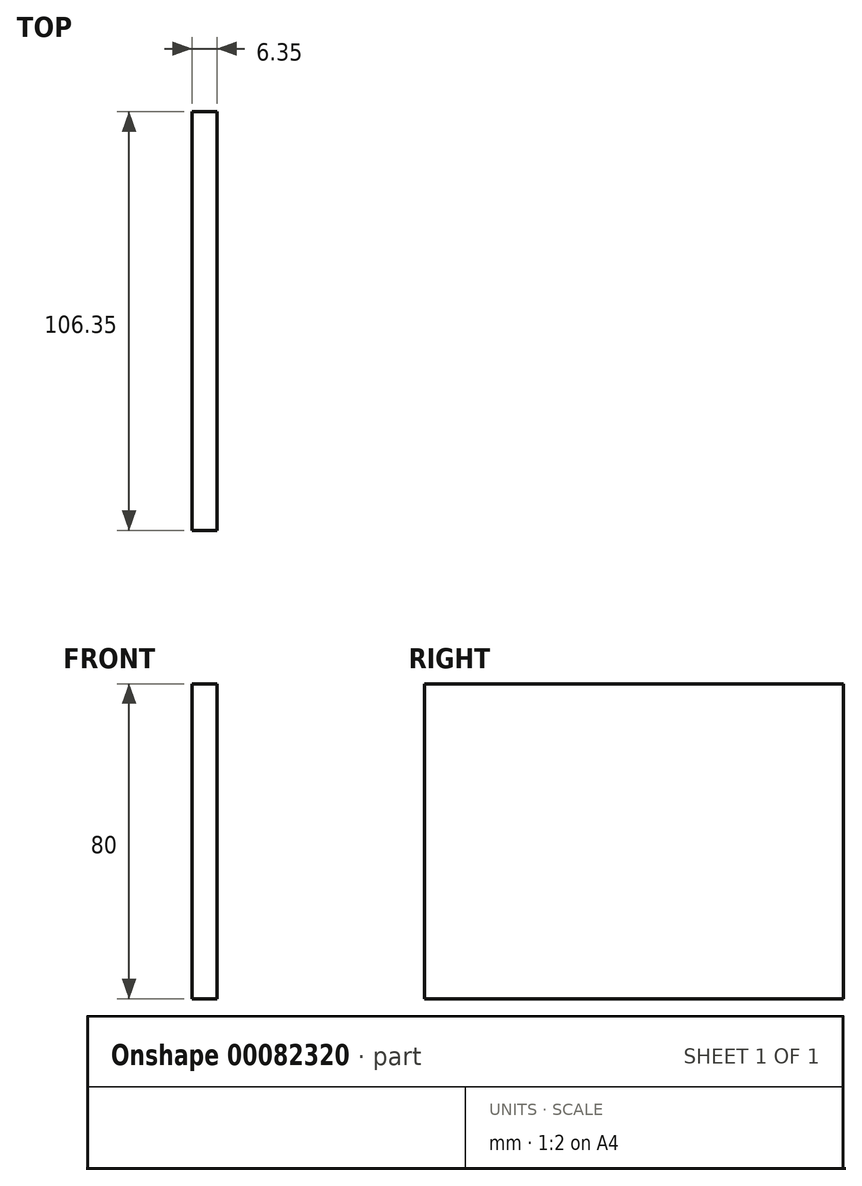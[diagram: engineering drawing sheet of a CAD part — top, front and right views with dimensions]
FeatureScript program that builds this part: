
annotation { "Feature Type Name" : "Feature", "Feature Type Description" : "" }
export const myFeature = defineFeature(function(context is Context, id is Id, definition is map)
    precondition{}
    {
        {
            var Q0;
            Q0=qCreatedBy(makeId("Right.planeOp"),FACE);
            var sketch = newSketch(context, id + "F0", { "sketchPlane" : qUnion([Q0])});
            skLineSegment(sketch, "E0.bottom", {"start": v(50, -37.5) * mm, "end": v(-50, -37.5) * mm});
            skLineSegment(sketch, "E0.top", {"start": v(50, 37.5) * mm, "end": v(-50, 37.5) * mm});
            skLineSegment(sketch, "E0.left", {"start": v(50, -37.5) * mm, "end": v(50, 37.5) * mm});
            skLineSegment(sketch, "E0.right", {"start": v(-50, -37.5) * mm, "end": v(-50, 37.5) * mm});
            skPoint(sketch, "E0.middle", {"position": v(0, 0) * mm});
            skCircle(sketch, "E1", {"center": v(-36.39, -27.5) * mm, "radius": 2.39 * mm});
            skCircle(sketch, "E2", {"center": v(-42.38, -27.5) * mm, "radius": 2.39 * mm});
            skLineSegment(sketch, "E3.bottom", {"start": v(50, 37.5) * mm, "end": v(56.35, 37.5) * mm});
            skLineSegment(sketch, "E3.top", {"start": v(50, -37.5) * mm, "end": v(56.35, -37.5) * mm});
            skLineSegment(sketch, "E3.left", {"start": v(50, 37.5) * mm, "end": v(50, -37.5) * mm});
            skLineSegment(sketch, "E3.right", {"start": v(56.35, 37.5) * mm, "end": v(56.35, -37.5) * mm});
            skLineSegment(sketch, "E4.bottom", {"start": v(-50, 37.5) * mm, "end": v(56.35, 37.5) * mm});
            skLineSegment(sketch, "E4.top", {"start": v(-50, 42.5) * mm, "end": v(56.35, 42.5) * mm});
            skLineSegment(sketch, "E4.left", {"start": v(-50, 37.5) * mm, "end": v(-50, 42.5) * mm});
            skLineSegment(sketch, "E4.right", {"start": v(56.35, 37.5) * mm, "end": v(56.35, 42.5) * mm});
            skSolve(sketch);
        }
        {
            var Q0;
            Q0 = qSketchRegion(id + "F0", true);
            var Q1;
            Q1=makeQuery(id+"F0.imprint","IMPRINT",FACE,{"disambiguationData":[TD([[makeQuery(id+"F0.imprint","IMPRINT",EDGE,{"derivedFrom":sQuery(id+"F0.wireOp",EDGE,"E2")}),1.0]])]});
            var Q2;
            Q2=makeQuery(id+"F0.imprint","IMPRINT",FACE,{"disambiguationData":[TD([[makeQuery(id+"F0.imprint","IMPRINT",EDGE,{"derivedFrom":sQuery(id+"F0.wireOp",EDGE,"E1")}),1.0]])]});
            extrude(context, id + "F1", {"entities" : qUnion([Q0, Q1, Q2]), "depth" : 6.35 * mm});
        }
    });
